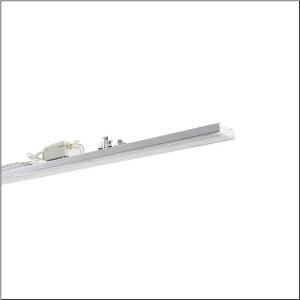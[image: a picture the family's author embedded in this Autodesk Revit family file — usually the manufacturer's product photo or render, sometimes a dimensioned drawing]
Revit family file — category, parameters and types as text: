
# Revit family: licross_r__21_recessed_ho_52tl12cn4c5m_6852
name_source: partatom
category: Lighting Fixtures
units: mm (PartAtom-declared; Revit-internal decimal feet)

## family parameters
Cut with Voids When Loaded = No
Host = Face
Light Source = No
Part Type = Normal
Room Calculation Point = No
Round Connector Dimension = Use Diameter
Shared = No

## types (1)
- --- (1 x LED, 12670 lm, 68.4 W, 4000K)
    Apparent Load = 68 VA
    CIE Flux Codes = 69 91 98 100 100
    Color Rendering = 80
    Color Temperature = 4000K
    Default Elevation = 1800 mm
    Description = Licross® 21 Recessed HO, luminaire insert, of sheet steel, galvanised, coil coated, white, length: 1.500mm, width: 66mm, height: 67mm, LED rated luminous flux: 12.670lm, light colour: 840, control gear: ON/OFF Multilumen, CLOi, control gear: ECG Multilumen, with plug, 3-pole, with phase selection, mains connection: 220..240V, AC, 50/60Hz, start of lifetime: 68W, end of service life: 83W, halogen-free wiring, primary optical cover: cover, of PMMA, light emission: direct distribution, primary light characteristic: symmetric, protection rating (complete): IP40, insulation class (complete): insulation class I (protective earthing), certification: CE, ENEC, VDE, UKCA, protection symbol: D if used in an environment without relevant dust loads with corresponding accessories, impact resistance: IK06, permissible ambient temperature for indoor applications: -35..+30°C, corresponds to IFS (International Featured Standards) requirements for safety and quality in the food industry, reducing of maximum allowable ambient temperature of 5°C with ceiling mounting, LABS conformity tested according to VDMA 24364:2018-05, packaging unit: 1 piece
    Height = 58 mm
    Lamp = 1 x LED
    Lamp Light Flux = 12670 lm
    Lamp Power = 68.4 W
    Lamp count = 1
    Length = 1500 mm
    Luminous efficacy = 185 lm/W
    Manufacturer = Siteco
    ModVariant = No
    Model = 52TL12CN4C5M
    Mounting Place = Ceiling
    Mounting Type = Pendant
    Number of Poles = 1
    OnlyDefault = Yes
    Power Factor = 1
    Product Name = Licross® 21 Recessed HO
    Product group = luminaire insert
    ProductGroupID = 901
    Protection Class = Protection class I
    Protection Degree = IP 40
    RLX_Detail_Level = 1
    RLX_Emergency_Light_Flux = 0 lm
    RLX_Emergency_Type = 0
    RLX_Emergency_Type_DB = No
    RlxData = <blob elided: 22361 chars, md5=2414f792>
    Socket = socket
    Standby Power = 0 W
    System Light Flux = 12670 lm
    System Power = 68 W
    Type Comments = factory setting: luminous flux: 100 % | (A | C | E) | 161 mA
    Type Image = l_1296930.jpg
    URL = http://relux.com
    VarID = @adj_040001
    Voltage = 0 V
    Weight = 0.00 kg
    Width = 66 mm

## geometry (parser evidence)
native form markers: Blend x4, Sweep x13
no freeform markers — native parametric forms only
